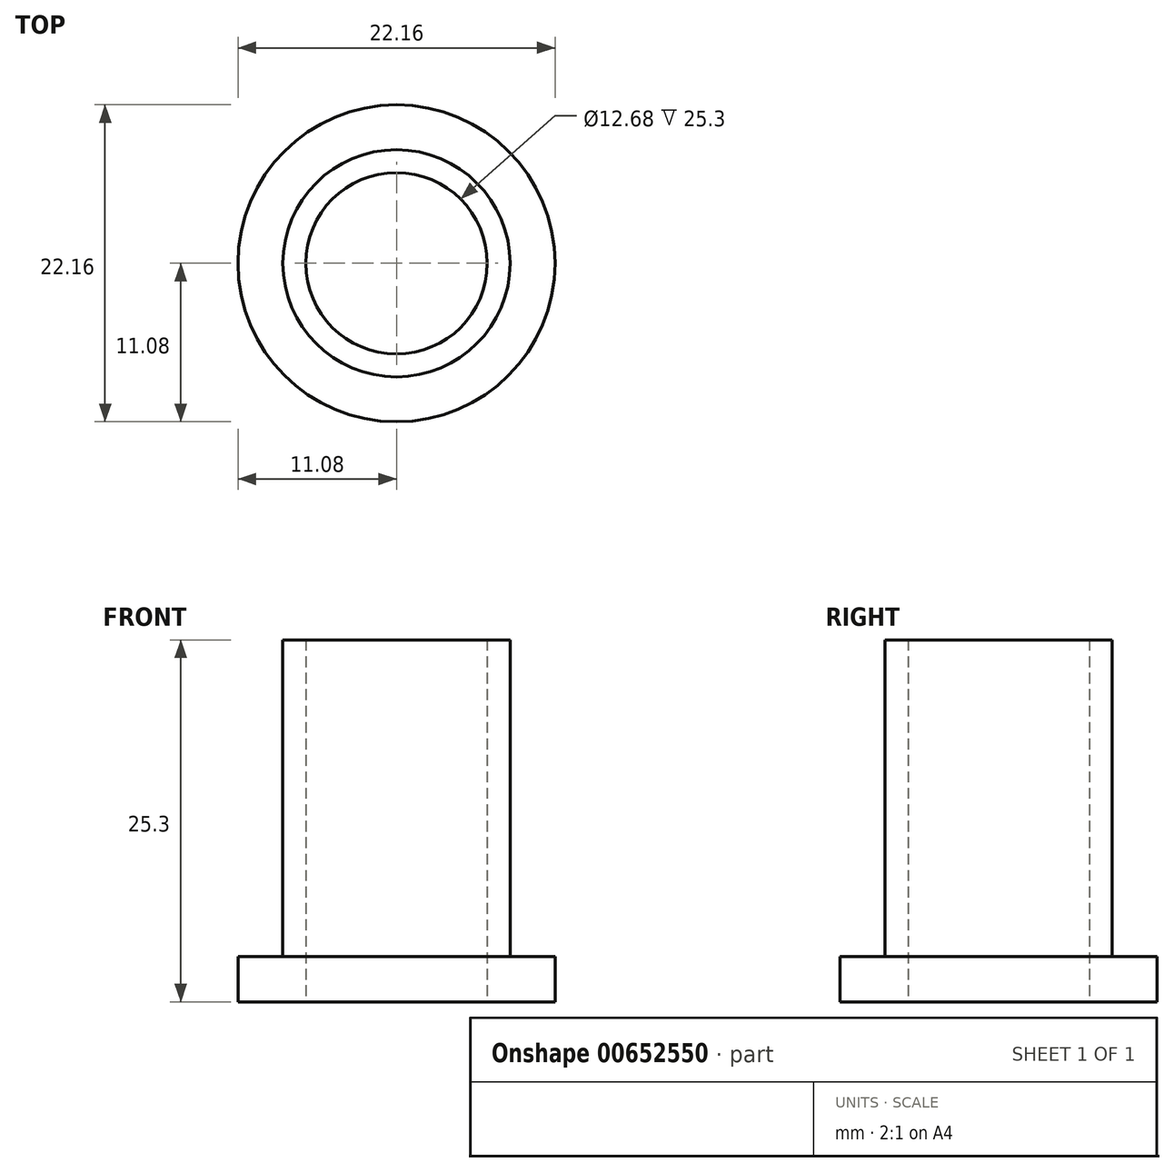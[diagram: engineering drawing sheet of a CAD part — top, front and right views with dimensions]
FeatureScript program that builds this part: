
annotation { "Feature Type Name" : "Feature", "Feature Type Description" : "" }
export const myFeature = defineFeature(function(context is Context, id is Id, definition is map)
    precondition{}
    {
        {
            var Q0;
            Q0=qCreatedBy(makeId("Top.planeOp"),FACE);
            var sketch = newSketch(context, id + "F0", { "sketchPlane" : qUnion([Q0])});
            skCircle(sketch, "E0", {"center": v(0, 0) * mm, "radius": 11.08 * mm});
            skCircle(sketch, "E1", {"center": v(0, 0) * mm, "radius": 7.94 * mm});
            skCircle(sketch, "E2", {"center": v(0, 0) * mm, "radius": 6.34 * mm});
            skSolve(sketch);
        }
        {
            var Q0;
            Q0=makeQuery(id+"F0.imprint","IMPRINT",FACE,{"disambiguationData":[TD([[makeQuery(id+"F0.imprint","IMPRINT",EDGE,{"derivedFrom":sQuery(id+"F0.wireOp",EDGE,"E0")}),1.0]])]});
            extrude(context, id + "F1", {"entities" : qUnion([Q0]), "depth" : 3.16 * mm, "offsetDistance" : 25 * mm});
        }
        {
            var Q0;
            Q0=makeQuery(id+"F0.imprint","IMPRINT",FACE,{"disambiguationData":[TD([[makeQuery(id+"F0.imprint","IMPRINT",EDGE,{"derivedFrom":sQuery(id+"F0.wireOp",EDGE,"E1")}),1.0]])]});
            extrude(context, id + "F2", {"entities" : qUnion([Q0]), "operationType" : NewBodyOperationType.ADD, "depth" : (3.16 + 22.14) * mm, "offsetDistance" : 25 * mm});
        }
    });
